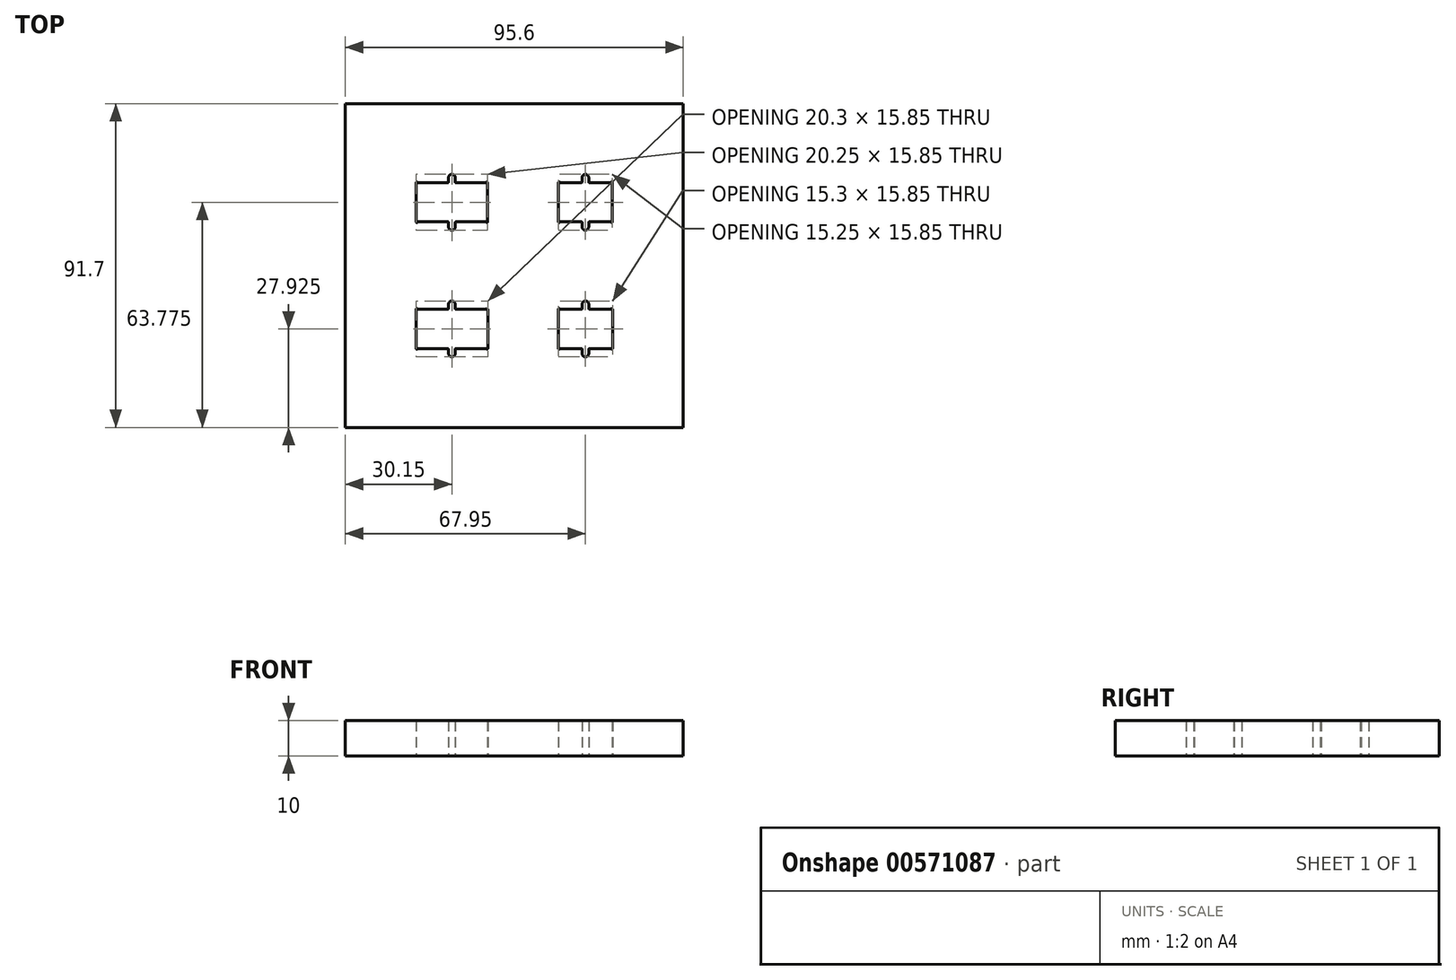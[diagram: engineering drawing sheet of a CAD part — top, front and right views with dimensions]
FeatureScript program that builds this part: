
annotation { "Feature Type Name" : "Feature", "Feature Type Description" : "" }
export const myFeature = defineFeature(function(context is Context, id is Id, definition is map)
    precondition{}
    {
        {
            var Q0;
            Q0=qCreatedBy(makeId("Top.planeOp"),FACE);
            var sketch = newSketch(context, id + "F0", { "sketchPlane" : qUnion([Q0])});
            skLineSegment(sketch, "E0.bottom", {"start": v(0, 0) * mm, "end": v(95.6, 0) * mm});
            skLineSegment(sketch, "E0.top", {"start": v(0, 91.7) * mm, "end": v(95.6, 91.7) * mm});
            skLineSegment(sketch, "E0.left", {"start": v(0, 0) * mm, "end": v(0, 91.7) * mm});
            skLineSegment(sketch, "E0.right", {"start": v(95.6, 0) * mm, "end": v(95.6, 91.7) * mm});
            skLineSegment(sketch, "E1.bottom", {"start": v(20.12, 22.47) * mm, "end": v(40.17, 22.47) * mm, "construction": true});
            skLineSegment(sketch, "E1.top", {"start": v(20.12, 33.37) * mm, "end": v(40.17, 33.37) * mm, "construction": true});
            skLineSegment(sketch, "E2", {"start": v(29.22, 33.7) * mm, "end": v(29.22, 34.92) * mm});
            skLineSegment(sketch, "E3", {"start": v(31.07, 34.92) * mm, "end": v(31.07, 33.7) * mm});
            skPoint(sketch, "E4", {"position": v(30.15, 33.37) * mm});
            skPoint(sketch, "E5", {"position": v(30.15, 34.92) * mm});
            skArc(sketch, "E6", {"start": v(29.22, 34.92) * mm, "mid": v(30.15, 35.85) * mm, "end": v(31.08, 34.92) * mm});
            skArc(sketch, "E7.filletArc", {"start": v(29.02, 33.5) * mm, "mid": v(29.17, 33.56) * mm, "end": v(29.22, 33.7) * mm});
            skArc(sketch, "E8.filletArc", {"start": v(31.07, 33.7) * mm, "mid": v(31.13, 33.56) * mm, "end": v(31.27, 33.5) * mm});
            skLineSegment(sketch, "E9", {"start": v(40.17, 33.37) * mm, "end": v(40.17, 22.47) * mm, "construction": true});
            skLineSegment(sketch, "E10", {"start": v(20.12, 33.37) * mm, "end": v(20.12, 22.47) * mm, "construction": true});
            skLineSegment(sketch, "E11.0", {"start": v(20.48, 33.5) * mm, "end": v(29.02, 33.5) * mm});
            skLineSegment(sketch, "E11.1", {"start": v(20, 33.5) * mm, "end": v(20, 22.35) * mm});
            skLineSegment(sketch, "E11.2", {"start": v(20.48, 22.35) * mm, "end": v(29.02, 22.35) * mm});
            skLineSegment(sketch, "E11.3", {"start": v(40.3, 33.5) * mm, "end": v(40.3, 22.35) * mm});
            skPoint(sketch, "E12", {"position": v(20.12, 27.92) * mm});
            skLineSegment(sketch, "E13.trimOffspring", {"start": v(31.27, 33.5) * mm, "end": v(39.82, 33.5) * mm});
            skLineSegment(sketch, "E14", {"start": v(20.12, 27.92) * mm, "end": v(40.17, 27.92) * mm, "construction": true});
            skLineSegment(sketch, "E15", {"start": v(30.15, 33.37) * mm, "end": v(30.15, 22.47) * mm, "construction": true});
            skArc(sketch, "E16.MirrorCS", {"start": v(31.07, 22.15) * mm, "mid": v(31.13, 22.3) * mm, "end": v(31.27, 22.35) * mm});
            skArc(sketch, "E17.MirrorCS", {"start": v(29.02, 22.35) * mm, "mid": v(29.17, 22.3) * mm, "end": v(29.22, 22.15) * mm});
            skLineSegment(sketch, "E18.MirrorCS", {"start": v(31.07, 20.93) * mm, "end": v(31.07, 22.15) * mm});
            skLineSegment(sketch, "E19.MirrorCS", {"start": v(29.22, 22.15) * mm, "end": v(29.22, 20.93) * mm});
            skPoint(sketch, "E20.MirrorP", {"position": v(30.15, 20.93) * mm});
            skArc(sketch, "E21.MirrorCS", {"start": v(29.22, 20.93) * mm, "mid": v(30.15, 20) * mm, "end": v(31.08, 20.93) * mm});
            skPoint(sketch, "E22.MirrorP", {"position": v(30.15, 22.47) * mm});
            skLineSegment(sketch, "E23.trimOffspring", {"start": v(31.27, 22.35) * mm, "end": v(39.82, 22.35) * mm});
            skArc(sketch, "E24", {"start": v(20.39, 33.57) * mm, "mid": v(20.17, 33.7) * mm, "end": v(20, 33.5) * mm});
            skPoint(sketch, "E25.visualSharp", {"position": v(20.4, 33.5) * mm});
            skArc(sketch, "E25.filletArc", {"start": v(20.39, 33.57) * mm, "mid": v(20.43, 33.52) * mm, "end": v(20.48, 33.5) * mm});
            skArc(sketch, "E26.MirrorCS", {"start": v(20.39, 22.28) * mm, "mid": v(20.43, 22.33) * mm, "end": v(20.48, 22.35) * mm});
            skArc(sketch, "E27.MirrorCS", {"start": v(20.39, 22.28) * mm, "mid": v(20.17, 22.15) * mm, "end": v(20, 22.35) * mm});
            skArc(sketch, "E28.MirrorCS", {"start": v(39.91, 22.28) * mm, "mid": v(39.87, 22.33) * mm, "end": v(39.82, 22.35) * mm});
            skArc(sketch, "E29.MirrorCS", {"start": v(39.91, 22.28) * mm, "mid": v(40.13, 22.15) * mm, "end": v(40.3, 22.35) * mm});
            skArc(sketch, "E30.MirrorCS", {"start": v(39.91, 33.57) * mm, "mid": v(39.87, 33.52) * mm, "end": v(39.82, 33.5) * mm});
            skArc(sketch, "E31.MirrorCS", {"start": v(39.91, 33.57) * mm, "mid": v(40.13, 33.7) * mm, "end": v(40.3, 33.5) * mm});
            skLineSegment(sketch, "E32.bottom", {"start": v(20.12, 58.32) * mm, "end": v(40.17, 58.32) * mm, "construction": true});
            skLineSegment(sketch, "E32.top", {"start": v(20.12, 69.22) * mm, "end": v(40.17, 69.22) * mm, "construction": true});
            skLineSegment(sketch, "E33", {"start": v(29.22, 69.52) * mm, "end": v(29.22, 70.77) * mm});
            skLineSegment(sketch, "E34", {"start": v(31.07, 70.77) * mm, "end": v(31.07, 69.52) * mm});
            skPoint(sketch, "E35", {"position": v(30.15, 69.22) * mm});
            skPoint(sketch, "E36", {"position": v(30.15, 70.77) * mm});
            skArc(sketch, "E37", {"start": v(29.22, 70.77) * mm, "mid": v(30.15, 71.7) * mm, "end": v(31.07, 70.77) * mm});
            skArc(sketch, "E38.filletArc", {"start": v(29.02, 69.32) * mm, "mid": v(29.17, 69.38) * mm, "end": v(29.22, 69.52) * mm});
            skArc(sketch, "E39.filletArc", {"start": v(31.07, 69.52) * mm, "mid": v(31.13, 69.38) * mm, "end": v(31.27, 69.32) * mm});
            skLineSegment(sketch, "E40", {"start": v(40.17, 69.22) * mm, "end": v(40.17, 58.32) * mm, "construction": true});
            skLineSegment(sketch, "E41", {"start": v(20.12, 69.22) * mm, "end": v(20.12, 58.32) * mm, "construction": true});
            skLineSegment(sketch, "E42.0", {"start": v(20.5, 69.32) * mm, "end": v(29.02, 69.32) * mm});
            skLineSegment(sketch, "E42.1", {"start": v(20.02, 69.32) * mm, "end": v(20.02, 58.22) * mm});
            skLineSegment(sketch, "E42.2", {"start": v(20.5, 58.22) * mm, "end": v(29.02, 58.22) * mm});
            skLineSegment(sketch, "E42.3", {"start": v(40.27, 69.32) * mm, "end": v(40.27, 58.22) * mm});
            skPoint(sketch, "E43", {"position": v(20.12, 63.77) * mm});
            skLineSegment(sketch, "E44.trimOffspring", {"start": v(31.27, 69.32) * mm, "end": v(39.8, 69.32) * mm});
            skLineSegment(sketch, "E45", {"start": v(20.12, 63.77) * mm, "end": v(40.17, 63.77) * mm, "construction": true});
            skLineSegment(sketch, "E46", {"start": v(30.15, 69.22) * mm, "end": v(30.15, 58.32) * mm, "construction": true});
            skArc(sketch, "E47.MirrorCS", {"start": v(31.07, 58.02) * mm, "mid": v(31.13, 58.17) * mm, "end": v(31.27, 58.22) * mm});
            skArc(sketch, "E48.MirrorCS", {"start": v(29.02, 58.22) * mm, "mid": v(29.17, 58.17) * mm, "end": v(29.22, 58.02) * mm});
            skLineSegment(sketch, "E49.MirrorCS", {"start": v(31.07, 56.77) * mm, "end": v(31.07, 58.02) * mm});
            skLineSegment(sketch, "E50.MirrorCS", {"start": v(29.22, 58.02) * mm, "end": v(29.22, 56.77) * mm});
            skPoint(sketch, "E51.MirrorP", {"position": v(30.15, 56.77) * mm});
            skArc(sketch, "E52.MirrorCS", {"start": v(29.22, 56.77) * mm, "mid": v(30.15, 55.85) * mm, "end": v(31.07, 56.77) * mm});
            skPoint(sketch, "E53.MirrorP", {"position": v(30.15, 58.32) * mm});
            skLineSegment(sketch, "E54.trimOffspring", {"start": v(31.27, 58.22) * mm, "end": v(39.8, 58.22) * mm});
            skArc(sketch, "E55", {"start": v(20.41, 69.4) * mm, "mid": v(20.2, 69.52) * mm, "end": v(20.02, 69.32) * mm});
            skPoint(sketch, "E56.visualSharp", {"position": v(20.42, 69.32) * mm});
            skArc(sketch, "E56.filletArc", {"start": v(20.41, 69.4) * mm, "mid": v(20.45, 69.34) * mm, "end": v(20.5, 69.32) * mm});
            skArc(sketch, "E57.MirrorCS", {"start": v(20.41, 58.16) * mm, "mid": v(20.45, 58.2) * mm, "end": v(20.5, 58.22) * mm});
            skArc(sketch, "E58.MirrorCS", {"start": v(20.41, 58.16) * mm, "mid": v(20.2, 58.03) * mm, "end": v(20.02, 58.22) * mm});
            skArc(sketch, "E59.MirrorCS", {"start": v(39.89, 58.16) * mm, "mid": v(39.85, 58.2) * mm, "end": v(39.8, 58.22) * mm});
            skArc(sketch, "E60.MirrorCS", {"start": v(39.89, 58.16) * mm, "mid": v(40.1, 58.03) * mm, "end": v(40.27, 58.22) * mm});
            skArc(sketch, "E61.MirrorCS", {"start": v(39.89, 69.4) * mm, "mid": v(39.85, 69.34) * mm, "end": v(39.8, 69.32) * mm});
            skArc(sketch, "E62.MirrorCS", {"start": v(39.89, 69.4) * mm, "mid": v(40.1, 69.52) * mm, "end": v(40.27, 69.32) * mm});
            skLineSegment(sketch, "E63.bottom", {"start": v(60.42, 22.47) * mm, "end": v(75.47, 22.47) * mm, "construction": true});
            skLineSegment(sketch, "E63.top", {"start": v(60.42, 33.37) * mm, "end": v(75.47, 33.37) * mm, "construction": true});
            skLineSegment(sketch, "E64", {"start": v(67.03, 33.7) * mm, "end": v(67.03, 34.92) * mm});
            skLineSegment(sketch, "E65", {"start": v(68.87, 34.92) * mm, "end": v(68.87, 33.7) * mm});
            skPoint(sketch, "E66", {"position": v(67.95, 33.37) * mm});
            skPoint(sketch, "E67", {"position": v(67.95, 34.92) * mm});
            skArc(sketch, "E68", {"start": v(67.02, 34.92) * mm, "mid": v(67.95, 35.85) * mm, "end": v(68.88, 34.92) * mm});
            skArc(sketch, "E69.filletArc", {"start": v(66.82, 33.5) * mm, "mid": v(66.97, 33.56) * mm, "end": v(67.03, 33.7) * mm});
            skArc(sketch, "E70.filletArc", {"start": v(68.88, 33.7) * mm, "mid": v(68.93, 33.56) * mm, "end": v(69.08, 33.5) * mm});
            skLineSegment(sketch, "E71", {"start": v(75.47, 33.37) * mm, "end": v(75.47, 22.47) * mm, "construction": true});
            skLineSegment(sketch, "E72", {"start": v(60.42, 33.37) * mm, "end": v(60.42, 22.47) * mm, "construction": true});
            skLineSegment(sketch, "E73.0", {"start": v(60.78, 33.5) * mm, "end": v(66.82, 33.5) * mm});
            skLineSegment(sketch, "E73.1", {"start": v(60.3, 33.5) * mm, "end": v(60.3, 22.35) * mm});
            skLineSegment(sketch, "E73.2", {"start": v(60.78, 22.35) * mm, "end": v(66.83, 22.35) * mm});
            skLineSegment(sketch, "E73.3", {"start": v(75.6, 33.5) * mm, "end": v(75.6, 22.35) * mm});
            skPoint(sketch, "E74", {"position": v(60.42, 27.92) * mm});
            skLineSegment(sketch, "E75.trimOffspring", {"start": v(69.08, 33.5) * mm, "end": v(75.12, 33.5) * mm});
            skLineSegment(sketch, "E76", {"start": v(60.42, 27.92) * mm, "end": v(75.47, 27.92) * mm, "construction": true});
            skLineSegment(sketch, "E77", {"start": v(67.95, 33.37) * mm, "end": v(67.95, 22.47) * mm, "construction": true});
            skArc(sketch, "E78.MirrorCS", {"start": v(68.88, 22.15) * mm, "mid": v(68.93, 22.3) * mm, "end": v(69.08, 22.35) * mm});
            skArc(sketch, "E79.MirrorCS", {"start": v(66.83, 22.35) * mm, "mid": v(66.97, 22.3) * mm, "end": v(67.03, 22.15) * mm});
            skLineSegment(sketch, "E80.MirrorCS", {"start": v(68.87, 20.93) * mm, "end": v(68.87, 22.15) * mm});
            skLineSegment(sketch, "E81.MirrorCS", {"start": v(67.03, 22.15) * mm, "end": v(67.03, 20.93) * mm});
            skPoint(sketch, "E82.MirrorP", {"position": v(67.95, 20.92) * mm});
            skArc(sketch, "E83.MirrorCS", {"start": v(67.02, 20.93) * mm, "mid": v(67.95, 20) * mm, "end": v(68.88, 20.93) * mm});
            skPoint(sketch, "E84.MirrorP", {"position": v(67.95, 22.47) * mm});
            skLineSegment(sketch, "E85.trimOffspring", {"start": v(69.08, 22.35) * mm, "end": v(75.12, 22.35) * mm});
            skArc(sketch, "E86", {"start": v(60.69, 33.57) * mm, "mid": v(60.47, 33.7) * mm, "end": v(60.3, 33.5) * mm});
            skPoint(sketch, "E87.visualSharp", {"position": v(60.7, 33.5) * mm});
            skArc(sketch, "E87.filletArc", {"start": v(60.69, 33.57) * mm, "mid": v(60.73, 33.52) * mm, "end": v(60.78, 33.5) * mm});
            skArc(sketch, "E88.MirrorCS", {"start": v(60.69, 22.28) * mm, "mid": v(60.73, 22.33) * mm, "end": v(60.78, 22.35) * mm});
            skArc(sketch, "E89.MirrorCS", {"start": v(60.69, 22.28) * mm, "mid": v(60.47, 22.15) * mm, "end": v(60.3, 22.35) * mm});
            skArc(sketch, "E90.MirrorCS", {"start": v(75.21, 22.28) * mm, "mid": v(75.17, 22.33) * mm, "end": v(75.12, 22.35) * mm});
            skArc(sketch, "E91.MirrorCS", {"start": v(75.21, 22.28) * mm, "mid": v(75.43, 22.15) * mm, "end": v(75.6, 22.35) * mm});
            skArc(sketch, "E92.MirrorCS", {"start": v(75.21, 33.57) * mm, "mid": v(75.17, 33.52) * mm, "end": v(75.12, 33.5) * mm});
            skArc(sketch, "E93.MirrorCS", {"start": v(75.21, 33.57) * mm, "mid": v(75.43, 33.7) * mm, "end": v(75.6, 33.5) * mm});
            skLineSegment(sketch, "E94.bottom", {"start": v(60.42, 58.32) * mm, "end": v(75.47, 58.32) * mm, "construction": true});
            skLineSegment(sketch, "E94.top", {"start": v(60.42, 69.22) * mm, "end": v(75.47, 69.22) * mm, "construction": true});
            skLineSegment(sketch, "E95", {"start": v(67.02, 69.52) * mm, "end": v(67.02, 70.77) * mm});
            skLineSegment(sketch, "E96", {"start": v(68.87, 70.77) * mm, "end": v(68.87, 69.52) * mm});
            skPoint(sketch, "E97", {"position": v(67.95, 69.22) * mm});
            skPoint(sketch, "E98", {"position": v(67.95, 70.77) * mm});
            skArc(sketch, "E99", {"start": v(67.02, 70.77) * mm, "mid": v(67.95, 71.7) * mm, "end": v(68.87, 70.77) * mm});
            skArc(sketch, "E100.filletArc", {"start": v(66.82, 69.32) * mm, "mid": v(66.97, 69.38) * mm, "end": v(67.02, 69.52) * mm});
            skArc(sketch, "E101.filletArc", {"start": v(68.87, 69.52) * mm, "mid": v(68.93, 69.38) * mm, "end": v(69.07, 69.32) * mm});
            skLineSegment(sketch, "E102", {"start": v(75.47, 69.22) * mm, "end": v(75.47, 58.32) * mm, "construction": true});
            skLineSegment(sketch, "E103", {"start": v(60.42, 69.22) * mm, "end": v(60.42, 58.32) * mm, "construction": true});
            skLineSegment(sketch, "E104.0", {"start": v(60.8, 69.32) * mm, "end": v(66.82, 69.32) * mm});
            skLineSegment(sketch, "E104.1", {"start": v(60.32, 69.32) * mm, "end": v(60.32, 58.22) * mm});
            skLineSegment(sketch, "E104.2", {"start": v(60.8, 58.22) * mm, "end": v(66.82, 58.22) * mm});
            skLineSegment(sketch, "E104.3", {"start": v(75.58, 69.32) * mm, "end": v(75.58, 58.22) * mm});
            skPoint(sketch, "E105", {"position": v(60.42, 63.77) * mm});
            skLineSegment(sketch, "E106.trimOffspring", {"start": v(69.07, 69.32) * mm, "end": v(75.1, 69.32) * mm});
            skLineSegment(sketch, "E107", {"start": v(60.42, 63.77) * mm, "end": v(75.47, 63.77) * mm, "construction": true});
            skLineSegment(sketch, "E108", {"start": v(67.95, 69.22) * mm, "end": v(67.95, 58.32) * mm, "construction": true});
            skArc(sketch, "E109.MirrorCS", {"start": v(68.87, 58.02) * mm, "mid": v(68.93, 58.17) * mm, "end": v(69.07, 58.22) * mm});
            skArc(sketch, "E110.MirrorCS", {"start": v(66.82, 58.22) * mm, "mid": v(66.97, 58.17) * mm, "end": v(67.02, 58.02) * mm});
            skLineSegment(sketch, "E111.MirrorCS", {"start": v(68.87, 56.77) * mm, "end": v(68.87, 58.02) * mm});
            skLineSegment(sketch, "E112.MirrorCS", {"start": v(67.02, 58.02) * mm, "end": v(67.02, 56.77) * mm});
            skPoint(sketch, "E113.MirrorP", {"position": v(67.95, 56.77) * mm});
            skArc(sketch, "E114.MirrorCS", {"start": v(67.02, 56.77) * mm, "mid": v(67.95, 55.85) * mm, "end": v(68.87, 56.77) * mm});
            skPoint(sketch, "E115.MirrorP", {"position": v(67.95, 58.32) * mm});
            skLineSegment(sketch, "E116.trimOffspring", {"start": v(69.07, 58.22) * mm, "end": v(75.1, 58.22) * mm});
            skArc(sketch, "E117", {"start": v(60.71, 69.4) * mm, "mid": v(60.5, 69.52) * mm, "end": v(60.32, 69.32) * mm});
            skPoint(sketch, "E118.visualSharp", {"position": v(60.72, 69.32) * mm});
            skArc(sketch, "E118.filletArc", {"start": v(60.71, 69.4) * mm, "mid": v(60.75, 69.34) * mm, "end": v(60.8, 69.32) * mm});
            skArc(sketch, "E119.MirrorCS", {"start": v(60.71, 58.16) * mm, "mid": v(60.75, 58.2) * mm, "end": v(60.8, 58.22) * mm});
            skArc(sketch, "E120.MirrorCS", {"start": v(60.71, 58.16) * mm, "mid": v(60.5, 58.03) * mm, "end": v(60.32, 58.22) * mm});
            skArc(sketch, "E121.MirrorCS", {"start": v(75.19, 58.16) * mm, "mid": v(75.15, 58.2) * mm, "end": v(75.1, 58.22) * mm});
            skArc(sketch, "E122.MirrorCS", {"start": v(75.19, 58.16) * mm, "mid": v(75.4, 58.03) * mm, "end": v(75.58, 58.22) * mm});
            skArc(sketch, "E123.MirrorCS", {"start": v(75.19, 69.4) * mm, "mid": v(75.15, 69.34) * mm, "end": v(75.1, 69.32) * mm});
            skArc(sketch, "E124.MirrorCS", {"start": v(75.19, 69.4) * mm, "mid": v(75.4, 69.52) * mm, "end": v(75.58, 69.32) * mm});
            skSolve(sketch);
        }
        {
            var Q0;
            Q0=makeQuery(id+"F0.imprint","IMPRINT",FACE,{"disambiguationData":[TD([[makeQuery(id+"F0.imprint","IMPRINT",EDGE,{"derivedFrom":sQuery(id+"F0.wireOp",EDGE,"E0.bottom")}),1.0]])]});
            extrude(context, id + "F1", {"entities" : qUnion([Q0]), "depth" : 10 * mm, "offsetDistance" : 25 * mm});
        }
    });
